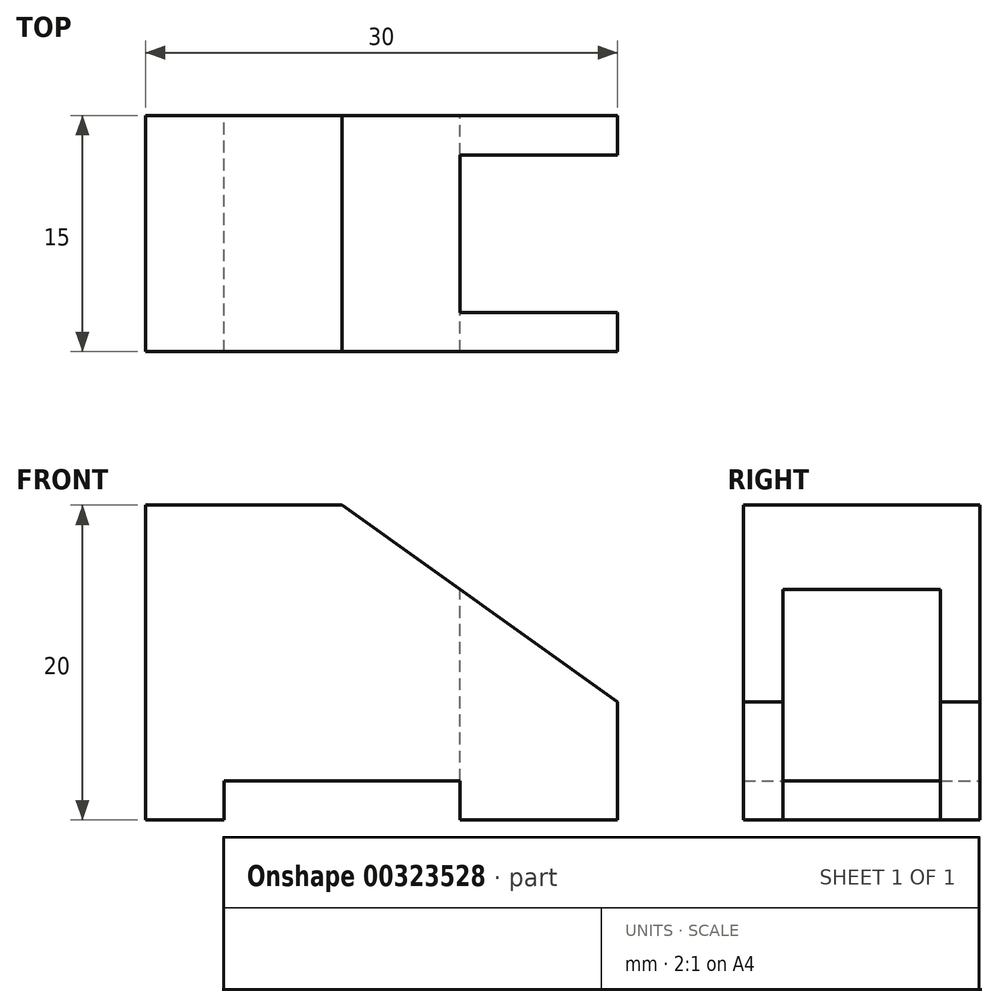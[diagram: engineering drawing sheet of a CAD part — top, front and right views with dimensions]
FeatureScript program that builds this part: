
annotation { "Feature Type Name" : "Feature", "Feature Type Description" : "" }
export const myFeature = defineFeature(function(context is Context, id is Id, definition is map)
    precondition{}
    {
        {
            var Q0;
            Q0=qCreatedBy(makeId("Front.planeOp"),FACE);
            var sketch = newSketch(context, id + "F0", { "sketchPlane" : qUnion([Q0])});
            skLineSegment(sketch, "E0", {"start": v(0, 0) * mm, "end": v(5, 0) * mm});
            skLineSegment(sketch, "E1", {"start": v(5, 0) * mm, "end": v(5, 2.5) * mm});
            skLineSegment(sketch, "E2", {"start": v(5, 2.5) * mm, "end": v(20, 2.5) * mm});
            skLineSegment(sketch, "E3", {"start": v(20, 2.5) * mm, "end": v(20, 0) * mm});
            skLineSegment(sketch, "E4", {"start": v(20, 0) * mm, "end": v(30, 0) * mm});
            skLineSegment(sketch, "E5", {"start": v(30, 0) * mm, "end": v(30, 7.5) * mm});
            skLineSegment(sketch, "E6", {"start": v(30, 7.5) * mm, "end": v(12.5, 20) * mm});
            skLineSegment(sketch, "E7", {"start": v(12.5, 20) * mm, "end": v(0, 20) * mm});
            skLineSegment(sketch, "E8", {"start": v(0, 20) * mm, "end": v(0, 0) * mm});
            skSolve(sketch);
        }
        {
            var Q0;
            Q0 = qSketchRegion(id + "F0", true);
            extrude(context, id + "F1", {"entities" : qUnion([Q0]), "depth" : 15 * mm});
        }
        {
            var Q0;
            Q0=makeQuery(id+"F1.opExtrude","SWEPT_FACE",FACE,{"disambiguationData":[OSD([sQuery(id+"F0.wireOp",EDGE,"E5")])]});
            var sketch = newSketch(context, id + "F2", { "sketchPlane" : qUnion([Q0])});
            skLineSegment(sketch, "E9.bottom", {"start": v(-12.5, 0) * mm, "end": v(-2.5, 0) * mm});
            skLineSegment(sketch, "E9.top", {"start": v(-12.5, 15) * mm, "end": v(-2.5, 15) * mm});
            skLineSegment(sketch, "E9.left", {"start": v(-12.5, 0) * mm, "end": v(-12.5, 15) * mm});
            skLineSegment(sketch, "E9.right", {"start": v(-2.5, 0) * mm, "end": v(-2.5, 15) * mm});
            skSolve(sketch);
        }
        {
            var Q0;
            {var subQ0=sQuery(id+"F2.wireOp",EDGE,"E9.top");Q0=makeQuery(id+"F2.imprint","IMPRINT",FACE,{"disambiguationData":[TD([[makeQuery(id+"F2.imprint","IMPRINT",EDGE,{"derivedFrom":subQ0}),-1.0]])]});}
            var Q1;
            {var subQ0=sQuery(id+"F2.wireOp",EDGE,"E9.bottom");Q1=makeQuery(id+"F2.imprint","IMPRINT",FACE,{"disambiguationData":[TD([[makeQuery(id+"F2.imprint","IMPRINT",EDGE,{"derivedFrom":subQ0}),1.0]])]});}
            extrude(context, id + "F3", {"entities" : qUnion([Q0, Q1]), "operationType" : NewBodyOperationType.REMOVE, "oppositeDirection" : true, "depth" : 10 * mm});
        }
    });
